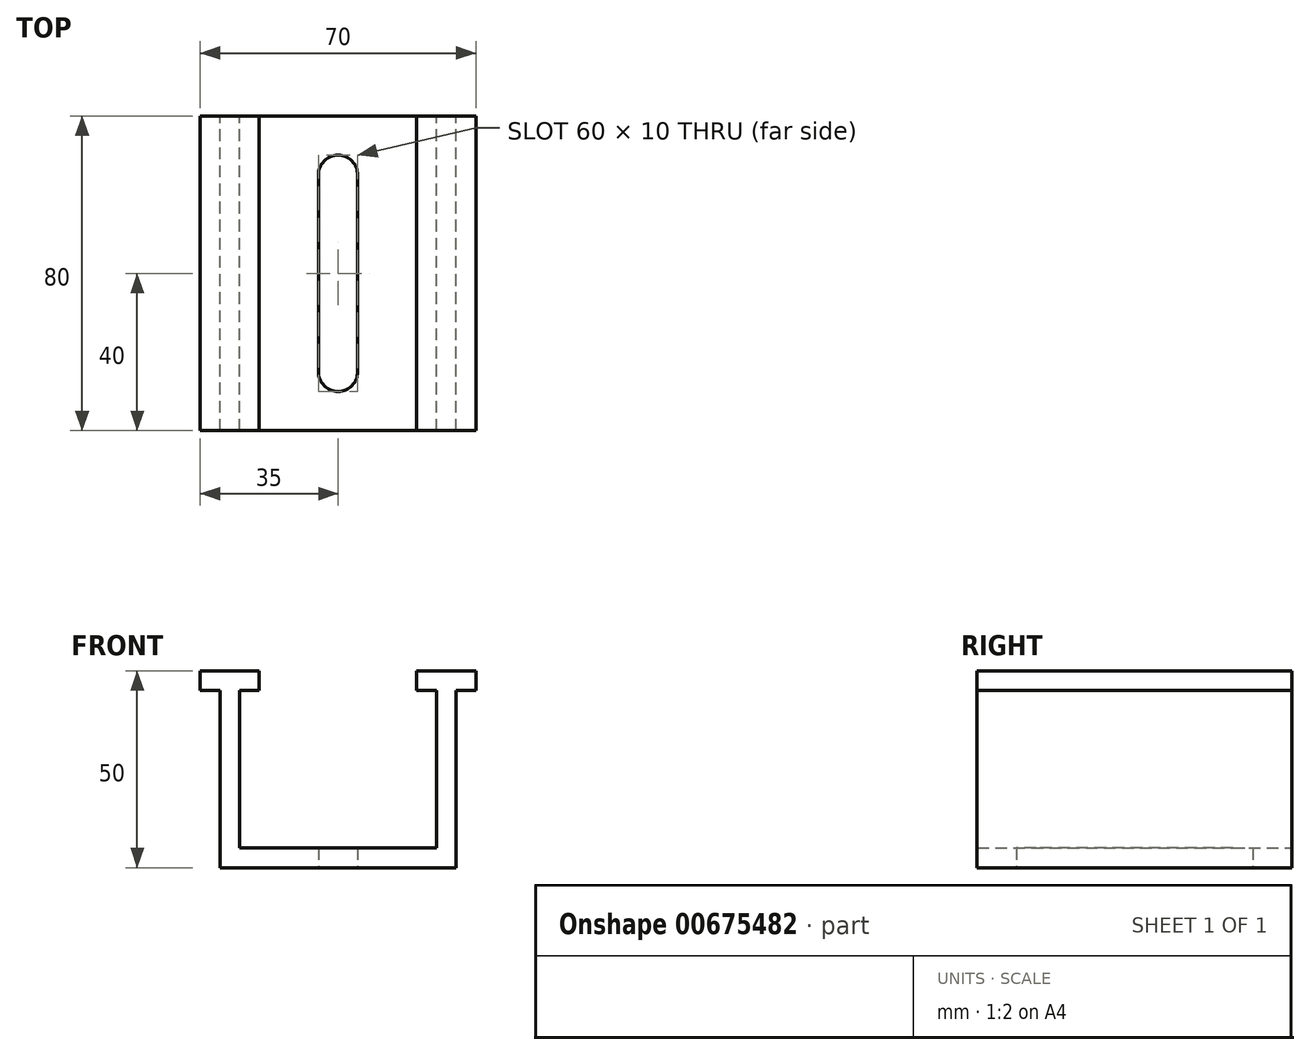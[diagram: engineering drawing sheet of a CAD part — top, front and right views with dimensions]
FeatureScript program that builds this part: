
annotation { "Feature Type Name" : "Feature", "Feature Type Description" : "" }
export const myFeature = defineFeature(function(context is Context, id is Id, definition is map)
    precondition{}
    {
        {
            var Q0;
            Q0=qCreatedBy(makeId("Front.planeOp"),FACE);
            var sketch = newSketch(context, id + "F0", { "sketchPlane" : qUnion([Q0])});
            skLineSegment(sketch, "E0.bottom", {"start": v(-17.58, -24.43) * mm, "end": v(42.42, -24.43) * mm});
            skLineSegment(sketch, "E0.top", {"start": v(-17.58, -29.43) * mm, "end": v(42.42, -29.43) * mm});
            skLineSegment(sketch, "E0.left", {"start": v(-17.58, -24.43) * mm, "end": v(-17.58, -29.43) * mm});
            skLineSegment(sketch, "E0.right", {"start": v(42.42, -24.43) * mm, "end": v(42.42, -29.43) * mm});
            skLineSegment(sketch, "E1.bottom", {"start": v(-17.58, -24.43) * mm, "end": v(-12.58, -24.43) * mm});
            skLineSegment(sketch, "E1.top", {"start": v(-17.58, 15.57) * mm, "end": v(-12.58, 15.57) * mm});
            skLineSegment(sketch, "E1.left", {"start": v(-17.58, -24.43) * mm, "end": v(-17.58, 15.57) * mm});
            skLineSegment(sketch, "E1.right", {"start": v(-12.58, -24.43) * mm, "end": v(-12.58, 15.57) * mm});
            skLineSegment(sketch, "E2.bottom", {"start": v(42.42, -24.43) * mm, "end": v(37.42, -24.43) * mm});
            skLineSegment(sketch, "E2.top", {"start": v(42.42, 15.57) * mm, "end": v(37.42, 15.57) * mm});
            skLineSegment(sketch, "E2.left", {"start": v(42.42, -24.43) * mm, "end": v(42.42, 15.57) * mm});
            skLineSegment(sketch, "E2.right", {"start": v(37.42, -24.43) * mm, "end": v(37.42, 15.57) * mm});
            skLineSegment(sketch, "E3.bottom", {"start": v(-22.58, 15.57) * mm, "end": v(-7.58, 15.57) * mm});
            skLineSegment(sketch, "E3.top", {"start": v(-22.58, 20.57) * mm, "end": v(-7.58, 20.57) * mm});
            skLineSegment(sketch, "E3.left", {"start": v(-22.58, 15.57) * mm, "end": v(-22.58, 20.57) * mm});
            skLineSegment(sketch, "E3.right", {"start": v(-7.58, 15.57) * mm, "end": v(-7.58, 20.57) * mm});
            skLineSegment(sketch, "E4.bottom", {"start": v(47.42, 15.57) * mm, "end": v(32.42, 15.57) * mm});
            skLineSegment(sketch, "E4.top", {"start": v(47.42, 20.57) * mm, "end": v(32.42, 20.57) * mm});
            skLineSegment(sketch, "E4.left", {"start": v(47.42, 15.57) * mm, "end": v(47.42, 20.57) * mm});
            skLineSegment(sketch, "E4.right", {"start": v(32.42, 15.57) * mm, "end": v(32.42, 20.57) * mm});
            skPoint(sketch, "E5", {"position": v(39.92, 15.57) * mm});
            skLineSegment(sketch, "E6", {"start": v(39.92, 15.57) * mm, "end": v(39.92, 15.57) * mm});
            skPoint(sketch, "E7", {"position": v(-15.08, 15.57) * mm});
            skLineSegment(sketch, "E8", {"start": v(-15.08, 15.57) * mm, "end": v(-15.08, 15.57) * mm});
            skSolve(sketch);
        }
        {
            var Q0;
            Q0 = qSketchRegion(id + "F0", true);
            extrude(context, id + "F1", {"entities" : qUnion([Q0]), "depth" : 80 * mm, "offsetDistance" : 25 * mm});
        }
        {
            var Q0;
            Q0=makeQuery(id+"F1.opExtrude","SWEPT_FACE",FACE,{"disambiguationData":[OSD([sQuery(id+"F0.wireOp",EDGE,"E0.top")])]});
            var sketch = newSketch(context, id + "F2", { "sketchPlane" : qUnion([Q0])});
            skLineSegment(sketch, "E9.left", {"start": v(7.42, 65) * mm, "end": v(7.42, 15) * mm});
            skLineSegment(sketch, "E9.right", {"start": v(17.42, 65) * mm, "end": v(17.42, 15) * mm});
            skArc(sketch, "E10", {"start": v(17.42, 65) * mm, "mid": v(12.42, 70) * mm, "end": v(7.42, 65) * mm});
            skArc(sketch, "E11", {"start": v(7.42, 15) * mm, "mid": v(12.42, 10) * mm, "end": v(17.42, 15) * mm});
            skPoint(sketch, "E12", {"position": v(7.42, 40) * mm});
            skPoint(sketch, "E13", {"position": v(-17.58, 40) * mm});
            skSolve(sketch);
        }
        {
            var Q0;
            Q0=makeQuery(id+"F2.imprint","IMPRINT",FACE,{"disambiguationData":[TD([[makeQuery(id+"F2.imprint","IMPRINT",EDGE,{"derivedFrom":sQuery(id+"F2.wireOp",EDGE,"E9.left")}),1.0]])]});
            extrude(context, id + "F3", {"entities" : qUnion([Q0]), "operationType" : NewBodyOperationType.REMOVE, "oppositeDirection" : true, "depth" : 25 * mm, "offsetDistance" : 25 * mm});
        }
    });
